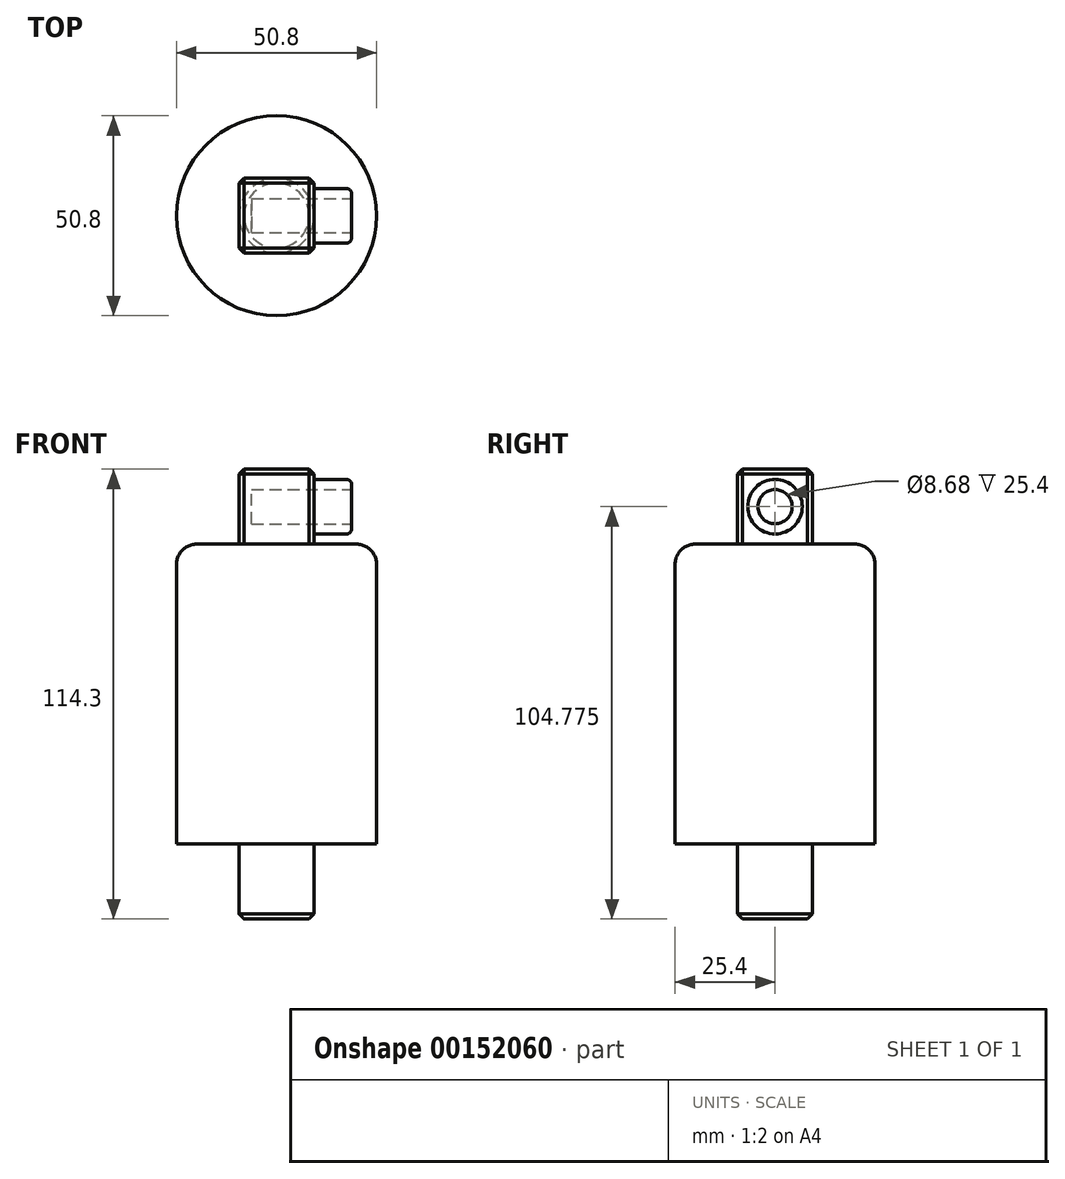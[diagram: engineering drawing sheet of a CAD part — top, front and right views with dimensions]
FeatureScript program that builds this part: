
annotation { "Feature Type Name" : "Feature", "Feature Type Description" : "" }
export const myFeature = defineFeature(function(context is Context, id is Id, definition is map)
    precondition{}
    {
        {
            var Q0;
            Q0=qCreatedBy(makeId("Top.planeOp"),FACE);
            var sketch = newSketch(context, id + "F0", { "sketchPlane" : qUnion([Q0])});
            skCircle(sketch, "E0", {"center": v(0, 0) * mm, "radius": 25.4 * mm});
            skSolve(sketch);
        }
        {
            var Q0;
            Q0 = qSketchRegion(id + "F0", true);
            extrude(context, id + "F1", {"entities" : qUnion([Q0]), "depth" : 76.2 * mm});
        }
        {
            var Q0;
            Q0=makeQuery(id+"F1.opExtrude","CAP_FACE",FACE,{"disambiguationData":[OSD([sQuery(id+"F0.wireOp",EDGE,"E0")])],"isStart":true});
            var sketch = newSketch(context, id + "F2", { "sketchPlane" : qUnion([Q0])});
            skCircle(sketch, "E1", {"center": v(0, 0) * mm, "radius": 9.53 * mm});
            skSolve(sketch);
        }
        {
            var Q0;
            Q0 = qSketchRegion(id + "F2", true);
            extrude(context, id + "F3", {"entities" : qUnion([Q0]), "operationType" : NewBodyOperationType.ADD, "depth" : 19.05 * mm});
        }
        {
            var Q0;
            Q0=makeQuery(id+"F1.opExtrude","CAP_EDGE",EDGE,{"disambiguationData":[OSD([sQuery(id+"F0.wireOp",EDGE,"E0")])],"isStart":false});
            fillet(context, id + "F4", {"entities" : qUnion([Q0]), "radius" : 5.08 * mm, "tangentPropagation" : true, "allowEdgeOverflow" : false});
        }
        {
            var Q0;
            Q0=makeQuery(id+"F3.opExtrude","CAP_EDGE",EDGE,{"disambiguationData":[OSD([sQuery(id+"F2.wireOp",EDGE,"E1")])],"isStart":false});
            chamfer(context, id + "F5", {"entities" : qUnion([Q0]), "width" : 1.27 * mm, "tangentPropagation" : true});
        }
        {
            var Q0;
            Q0=makeQuery(id+"F1.opExtrude","CAP_FACE",FACE,{"disambiguationData":[OSD([sQuery(id+"F0.wireOp",EDGE,"E0")])],"isStart":false});
            var sketch = newSketch(context, id + "F6", { "sketchPlane" : qUnion([Q0])});
            skLineSegment(sketch, "E2.bottom", {"start": v(9.53, 9.52) * mm, "end": v(-9.52, 9.53) * mm});
            skLineSegment(sketch, "E2.top", {"start": v(9.52, -9.53) * mm, "end": v(-9.53, -9.52) * mm});
            skLineSegment(sketch, "E2.left", {"start": v(9.53, 9.52) * mm, "end": v(9.52, -9.53) * mm});
            skLineSegment(sketch, "E2.right", {"start": v(-9.52, 9.53) * mm, "end": v(-9.53, -9.52) * mm});
            skPoint(sketch, "E2.middle", {"position": v(0, 0) * mm});
            skSolve(sketch);
        }
        {
            var Q0;
            Q0 = qSketchRegion(id + "F6", true);
            extrude(context, id + "F7", {"entities" : qUnion([Q0]), "operationType" : NewBodyOperationType.ADD, "depth" : 19.05 * mm});
        }
        {
            var Q0;
            Q0=makeQuery(id+"F7.opExtrude","SWEPT_FACE",FACE,{"disambiguationData":[OSD([sQuery(id+"F6.wireOp",EDGE,"E2.left")])]});
            var sketch = newSketch(context, id + "F8", { "sketchPlane" : qUnion([Q0])});
            skCircle(sketch, "E3", {"center": v(0, 85.73) * mm, "radius": 6.93 * mm});
            skPoint(sketch, "E3.centerSnap0", {"position": v(-9.53, 85.73) * mm});
            skPoint(sketch, "E3.centerSnap1", {"position": v(0, 76.2) * mm});
            skSolve(sketch);
        }
        {
            var Q0;
            Q0 = qSketchRegion(id + "F8", true);
            extrude(context, id + "F9", {"entities" : qUnion([Q0]), "operationType" : NewBodyOperationType.ADD, "depth" : 9.52 * mm});
        }
        {
            var Q0;
            Q0=makeQuery(id+"F9.opExtrude","CAP_FACE",FACE,{"disambiguationData":[OSD([sQuery(id+"F8.wireOp",EDGE,"E3")])],"isStart":false});
            var sketch = newSketch(context, id + "F10", { "sketchPlane" : qUnion([Q0])});
            skCircle(sketch, "E4", {"center": v(0, 85.73) * mm, "radius": 4.34 * mm});
            skSolve(sketch);
        }
        {
            var Q0;
            Q0 = qSketchRegion(id + "F10", true);
            extrude(context, id + "F11", {"entities" : qUnion([Q0]), "operationType" : NewBodyOperationType.REMOVE, "oppositeDirection" : true, "depth" : 25.4 * mm});
        }
        {
            var Q0;
            Q0=makeQuery(id+"F7.opExtrude","CAP_EDGE",EDGE,{"disambiguationData":[OSD([sQuery(id+"F6.wireOp",EDGE,"E2.top")])],"isStart":false});
            var Q1;
            Q1=makeQuery(id+"F7.opExtrude","SWEPT_EDGE",EDGE,{"disambiguationData":[OSD([sQuery(id+"F6.wireOp",EDGE,"E2.top"),sQuery(id+"F6.wireOp",EDGE,"E2.right")])]});
            var Q2;
            Q2=makeQuery(id+"F7.opExtrude","SWEPT_EDGE",EDGE,{"disambiguationData":[OSD([sQuery(id+"F6.wireOp",EDGE,"E2.top"),sQuery(id+"F6.wireOp",EDGE,"E2.left")])]});
            var Q3;
            Q3=makeQuery(id+"F7.opExtrude","SWEPT_EDGE",EDGE,{"disambiguationData":[OSD([sQuery(id+"F6.wireOp",EDGE,"E2.bottom"),sQuery(id+"F6.wireOp",EDGE,"E2.right")])]});
            var Q4;
            Q4=makeQuery(id+"F7.opExtrude","CAP_EDGE",EDGE,{"disambiguationData":[OSD([sQuery(id+"F6.wireOp",EDGE,"E2.right")])],"isStart":false});
            var Q5;
            Q5=makeQuery(id+"F7.opExtrude","SWEPT_EDGE",EDGE,{"disambiguationData":[OSD([sQuery(id+"F6.wireOp",EDGE,"E2.bottom"),sQuery(id+"F6.wireOp",EDGE,"E2.left")])]});
            var Q6;
            Q6=makeQuery(id+"F7.opExtrude","CAP_EDGE",EDGE,{"disambiguationData":[OSD([sQuery(id+"F6.wireOp",EDGE,"E2.bottom")])],"isStart":false});
            var Q7;
            Q7=makeQuery(id+"F7.opExtrude","CAP_EDGE",EDGE,{"disambiguationData":[OSD([sQuery(id+"F6.wireOp",EDGE,"E2.left")])],"isStart":false});
            chamfer(context, id + "F12", {"entities" : qUnion([Q0, Q1, Q2, Q3, Q4, Q5, Q6, Q7]), "width" : 1.27 * mm, "tangentPropagation" : true});
        }
        {
            var Q0;
            Q0=makeQuery(id+"F9.opExtrude","CAP_EDGE",EDGE,{"disambiguationData":[OSD([sQuery(id+"F8.wireOp",EDGE,"E3")])],"isStart":false});
            fillet(context, id + "F13", {"entities" : qUnion([Q0]), "radius" : 1.27 * mm, "tangentPropagation" : true, "allowEdgeOverflow" : false});
        }
    });
